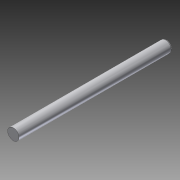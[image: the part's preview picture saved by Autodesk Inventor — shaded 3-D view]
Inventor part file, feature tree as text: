
AUTODESK INVENTOR PART (.ipt)
format: ipt  version: 2016 (Build 200138000, 138)  size: 82,944 bytes
history: native  units: mm
features: fillet x2, extrude x1, hole x1, sketch x1
ambient origin geometry x8: Origin, YZ Plane, XZ Plane, XY Plane, X Axis, Y Axis, Z Axis, Center Point
bodies: Solid1 (feature_tree)
feature tree (5):
  extrude  "Extrusion1"  Depth=68.0mm TaperAngle=0.0deg
  fillet  "Fillet1"  Radius=0.5mm
  hole  "Hole1"  [1 undecoded]
  fillet  "Fillet2"  Radius=0.25mm
  sketch  "Sketch1"  dims[d0=5.0mm d1=68.0mm d2=0.0mm d3=0.5mm d4=10.0mm d5=10.0mm d6=2.0mm d7=6.0mm d8=4.0mm d9=2.0mm d10=90.0deg d11=10.0mm d12=0.0mm d13=0.25mm]
note: 1 required parameter value undecoded (feature->parameter linkage not recoverable at this tier; creation-order binding heuristic only, values carry confidence <= 0.55)
